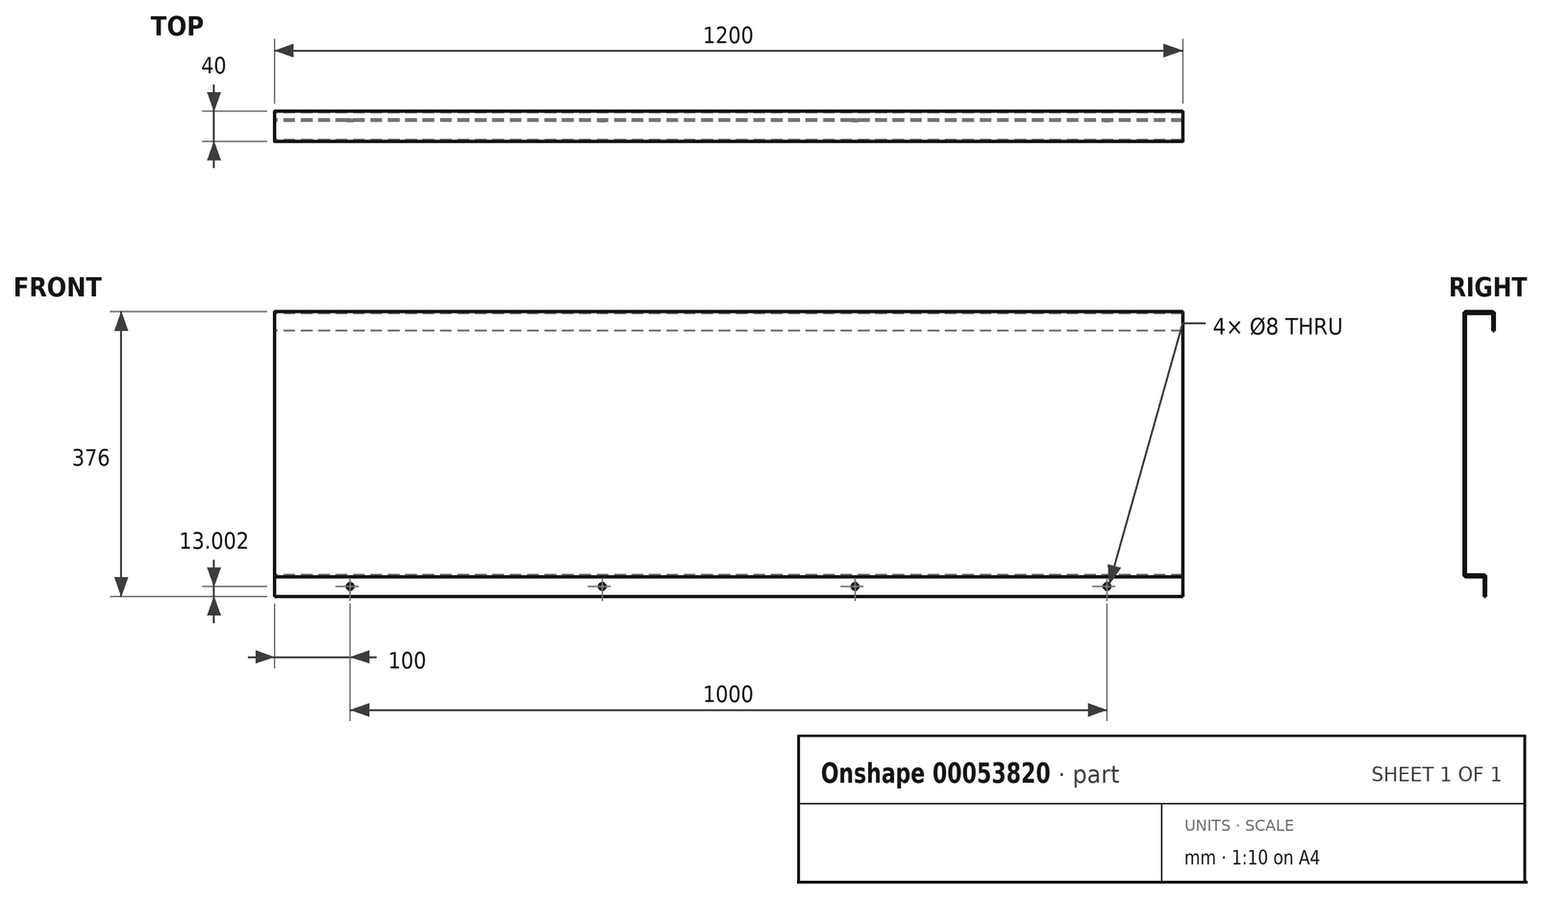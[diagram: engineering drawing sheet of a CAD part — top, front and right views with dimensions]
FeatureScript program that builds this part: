
annotation { "Feature Type Name" : "Feature", "Feature Type Description" : "" }
export const myFeature = defineFeature(function(context is Context, id is Id, definition is map)
    precondition{}
    {
        {
            var Q0;
            Q0=qCreatedBy(makeId("Right.planeOp"),FACE);
            var sketch = newSketch(context, id + "F0", { "sketchPlane" : qUnion([Q0])});
            skLineSegment(sketch, "E0", {"start": v(0, 0) * mm, "end": v(0, 430) * mm, "construction": true});
            skLineSegment(sketch, "E1", {"start": v(0, 0) * mm, "end": v(-250, 0) * mm, "construction": true});
            skLineSegment(sketch, "E2", {"start": v(-18.84, 404.8) * mm, "end": v(-18.84, 427.8) * mm});
            skLineSegment(sketch, "E3", {"start": v(-18.84, 427.8) * mm, "end": v(-54.84, 427.8) * mm});
            skLineSegment(sketch, "E4", {"start": v(-54.84, 427.8) * mm, "end": v(-54.84, 81.8) * mm});
            skLineSegment(sketch, "E5", {"start": v(-54.84, 81.8) * mm, "end": v(-27.84, 81.8) * mm});
            skLineSegment(sketch, "E6.0", {"start": v(-56.84, 79.8) * mm, "end": v(-29.84, 79.8) * mm});
            skLineSegment(sketch, "E6.1", {"start": v(-56.84, 429.8) * mm, "end": v(-56.84, 79.8) * mm});
            skLineSegment(sketch, "E6.2", {"start": v(-16.84, 429.8) * mm, "end": v(-56.84, 429.8) * mm});
            skLineSegment(sketch, "E6.3", {"start": v(-16.84, 404.8) * mm, "end": v(-16.84, 429.8) * mm});
            skLineSegment(sketch, "E7", {"start": v(-27.84, 81.8) * mm, "end": v(-27.84, 53.8) * mm});
            skLineSegment(sketch, "E8", {"start": v(-29.84, 79.8) * mm, "end": v(-29.84, 53.8) * mm});
            skLineSegment(sketch, "E9", {"start": v(-16.84, 404.8) * mm, "end": v(-18.84, 404.8) * mm});
            skLineSegment(sketch, "E10", {"start": v(-27.84, 53.8) * mm, "end": v(-29.84, 53.8) * mm});
            skSolve(sketch);
        }
        {
            var Q0;
            Q0=makeQuery(id+"F0.imprint","IMPRINT",FACE,{"disambiguationData":[TD([[makeQuery(id+"F0.imprint","IMPRINT",EDGE,{"derivedFrom":sQuery(id+"F0.wireOp",EDGE,"97aded3f-c788-494d-ab92-4e00cf807f6c")}),-1.0]])]});
            var Q1;
            Q1=makeQuery(id+"F0.imprint","IMPRINT",FACE,{"disambiguationData":[TD([[makeQuery(id+"F0.imprint","IMPRINT",EDGE,{"derivedFrom":sQuery(id+"F0.wireOp",EDGE,"E2")}),-1.0]])]});
            extrude(context, id + "F1", {"entities" : qUnion([Q0, Q1]), "depth" : 1200 * mm});
        }
        {
            var Q0;
            Q0=makeQuery(id+"F1.opExtrude","SWEPT_FACE",FACE,{"disambiguationData":[OSD([sQuery(id+"F0.wireOp",EDGE,"E8")])]});
            var sketch = newSketch(context, id + "F2", { "sketchPlane" : qUnion([Q0])});
            skLineSegment(sketch, "E11", {"start": v(0, 66.8) * mm, "end": v(1200, 66.8) * mm});
            skLineSegment(sketch, "E12", {"start": v(1100, 79.8) * mm, "end": v(1100, 53.8) * mm});
            skLineSegment(sketch, "E13", {"start": v(767, 79.8) * mm, "end": v(767, 53.8) * mm});
            skPoint(sketch, "E14", {"position": v(433, 66.8) * mm});
            skPoint(sketch, "E15", {"position": v(767, 66.8) * mm});
            skPoint(sketch, "E16", {"position": v(1100, 66.8) * mm});
            skLineSegment(sketch, "E17", {"start": v(433, 79.8) * mm, "end": v(433, 53.8) * mm});
            skLineSegment(sketch, "E18", {"start": v(100, 79.8) * mm, "end": v(100, 53.8) * mm});
            skPoint(sketch, "E19", {"position": v(100, 66.8) * mm});
            skSolve(sketch);
        }
        {
            var Q0;
            Q0=sQuery(id+"F2.wireOp",VERTEX,"E14");
            var Q1;
            Q1=sQuery(id+"F2.wireOp",VERTEX,"E15");
            var Q2;
            Q2=sQuery(id+"F2.wireOp",VERTEX,"E16");
            var Q3;
            Q3=sQuery(id+"F2.wireOp",VERTEX,"E19");
            var Q4;
            Q4=makeQuery(id+"F1.opExtrude","SWEPT_BODY",BODY,{"disambiguationData":[OSD([sQuery(id+"F0.wireOp",EDGE,"E2"),sQuery(id+"F0.wireOp",EDGE,"E3"),sQuery(id+"F0.wireOp",EDGE,"E4"),sQuery(id+"F0.wireOp",EDGE,"E5"),sQuery(id+"F0.wireOp",EDGE,"E6.0"),sQuery(id+"F0.wireOp",EDGE,"E6.1"),sQuery(id+"F0.wireOp",EDGE,"E6.2"),sQuery(id+"F0.wireOp",EDGE,"E6.3"),sQuery(id+"F0.wireOp",EDGE,"E7"),sQuery(id+"F0.wireOp",EDGE,"E8"),sQuery(id+"F0.wireOp",EDGE,"E9"),sQuery(id+"F0.wireOp",EDGE,"E10")])]});
            hole(context, id + "F3", {"style" : HoleStyle.SIMPLE, "holeDiameter" : 8 * mm, "endStyle" : HoleEndStyle.THROUGH, "locations" : qUnion([Q0, Q1, Q2, Q3]), "scope" : qUnion([Q4])});
        }
        {
            var Q0;
            Q0=makeQuery(id+"F1.opExtrude","SWEPT_EDGE",EDGE,{"disambiguationData":[OSD([sQuery(id+"F0.wireOp",EDGE,"E6.1"),sQuery(id+"F0.wireOp",EDGE,"E6.2")])]});
            var Q1;
            Q1=makeQuery(id+"F1.opExtrude","SWEPT_EDGE",EDGE,{"disambiguationData":[OSD([sQuery(id+"F0.wireOp",EDGE,"E6.2"),sQuery(id+"F0.wireOp",EDGE,"E6.3")])]});
            var Q2;
            Q2=makeQuery(id+"F1.opExtrude","SWEPT_EDGE",EDGE,{"disambiguationData":[OSD([sQuery(id+"F0.wireOp",EDGE,"E6.0"),sQuery(id+"F0.wireOp",EDGE,"E6.1")])]});
            var Q3;
            Q3=makeQuery(id+"F1.opExtrude","SWEPT_EDGE",EDGE,{"disambiguationData":[OSD([sQuery(id+"F0.wireOp",EDGE,"E5"),sQuery(id+"F0.wireOp",EDGE,"E7")])]});
            var Q4;
            Q4=makeQuery(id+"F1.opExtrude","SWEPT_EDGE",EDGE,{"disambiguationData":[OSD([sQuery(id+"F0.wireOp",EDGE,"E4"),sQuery(id+"F0.wireOp",EDGE,"E5")])]});
            var Q5;
            Q5=makeQuery(id+"F1.opExtrude","SWEPT_EDGE",EDGE,{"disambiguationData":[OSD([sQuery(id+"F0.wireOp",EDGE,"E6.0"),sQuery(id+"F0.wireOp",EDGE,"E8")])]});
            var Q6;
            Q6=makeQuery(id+"F1.opExtrude","SWEPT_EDGE",EDGE,{"disambiguationData":[OSD([sQuery(id+"F0.wireOp",EDGE,"E2"),sQuery(id+"F0.wireOp",EDGE,"E3")])]});
            var Q7;
            Q7=makeQuery(id+"F1.opExtrude","SWEPT_EDGE",EDGE,{"disambiguationData":[OSD([sQuery(id+"F0.wireOp",EDGE,"E3"),sQuery(id+"F0.wireOp",EDGE,"E4")])]});
            fillet(context, id + "F4", {"entities" : qUnion([Q0, Q1, Q2, Q3, Q4, Q5, Q6, Q7]), "radius" : 2 * mm, "tangentPropagation" : true, "allowEdgeOverflow" : false});
        }
    });
